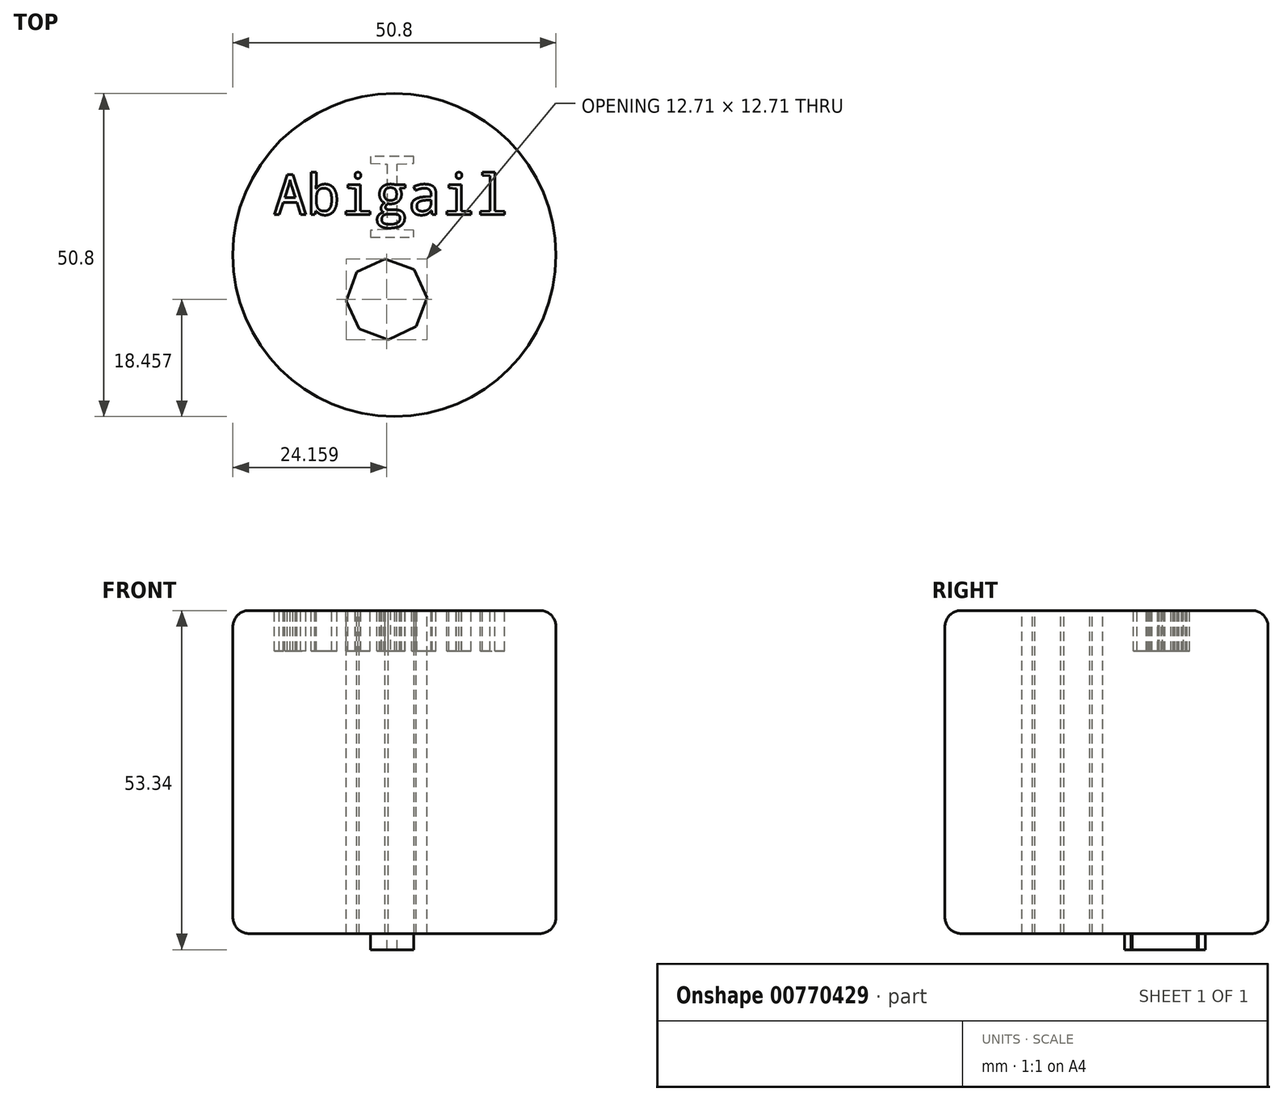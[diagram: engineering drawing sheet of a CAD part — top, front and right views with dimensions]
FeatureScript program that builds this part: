
annotation { "Feature Type Name" : "Feature", "Feature Type Description" : "" }
export const myFeature = defineFeature(function(context is Context, id is Id, definition is map)
    precondition{}
    {
        {
            var Q0;
            Q0=qCreatedBy(makeId("Top.planeOp"),FACE);
            var sketch = newSketch(context, id + "F0", { "sketchPlane" : qUnion([Q0])});
            skCircle(sketch, "E0", {"center": v(0, 0) * mm, "radius": 25.4 * mm});
            skSolve(sketch);
        }
        {
            var Q0;
            Q0 = qSketchRegion(id + "F0", true);
            extrude(context, id + "F1", {"entities" : qUnion([Q0]), "depth" : 50.8 * mm, "offsetDistance" : 25.4 * mm});
        }
        {
            var Q0;
            Q0=makeQuery(id+"F1.opExtrude","CAP_FACE",FACE,{"disambiguationData":[OSD([sQuery(id+"F0.wireOp",EDGE,"E0")])],"isStart":false});
            var sketch = newSketch(context, id + "F2", { "sketchPlane" : qUnion([Q0])});
            skText(sketch, "E1", { "text": "Abigail", "fontName": "DroidSansMono.ttf"});
            const initialGuessF2  = {"E1": [-0.01905, 0.00635, 1, 0, 0.00635]};
            skSetInitialGuess(sketch, initialGuessF2);
            skSolve(sketch);
        }
        {
            var Q0;
            Q0 = qSketchRegion(id + "F2", true);
            extrude(context, id + "F3", {"entities" : qUnion([Q0]), "operationType" : NewBodyOperationType.REMOVE, "oppositeDirection" : true, "depth" : 6.35 * mm, "offsetDistance" : 25.4 * mm});
        }
        {
            var Q0;
            {var subQ0=sQuery(id+"F0.wireOp",EDGE,"E0");Q0=makeQuery(id+"F3.boolean.opBoolean","SPLIT",FACE,{"disambiguationData":[TD([makeQuery(id+"F1.opExtrude","SWEPT_FACE",FACE,{"disambiguationData":[OSD([subQ0])]})])],"derivedFrom":makeQuery(id+"F1.opExtrude","CAP_FACE",FACE,{"disambiguationData":[OSD([subQ0])],"isStart":false})});}
            var sketch = newSketch(context, id + "F4", { "sketchPlane" : qUnion([Q0])});
            skCircle(sketch, "E2.cCircle", {"center": v(-1.24, -6.94) * mm, "radius": 5.88 * mm, "construction": true});
            skLineSegment(sketch, "E2.0", {"start": v(5.11, -6.68) * mm, "end": v(3.44, -11.25) * mm});
            skLineSegment(sketch, "E2.1", {"start": v(3.44, -11.25) * mm, "end": v(-0.98, -13.3) * mm});
            skLineSegment(sketch, "E2.2", {"start": v(-0.98, -13.3) * mm, "end": v(-5.55, -11.62) * mm});
            skLineSegment(sketch, "E2.3", {"start": v(-5.55, -11.62) * mm, "end": v(-7.6, -7.2) * mm});
            skLineSegment(sketch, "E2.4", {"start": v(-7.6, -7.2) * mm, "end": v(-5.92, -2.63) * mm});
            skLineSegment(sketch, "E2.5", {"start": v(-5.92, -2.63) * mm, "end": v(-1.5, -0.59) * mm});
            skLineSegment(sketch, "E2.6", {"start": v(-1.5, -0.59) * mm, "end": v(3.07, -2.26) * mm});
            skLineSegment(sketch, "E2.7", {"start": v(3.07, -2.26) * mm, "end": v(5.11, -6.68) * mm});
            skPoint(sketch, "E2.0.midPoint", {"position": v(4.28, -8.97) * mm});
            skSolve(sketch);
        }
        {
            var Q0;
            Q0 = qSketchRegion(id + "F4", true);
            extrude(context, id + "F5", {"entities" : qUnion([Q0]), "operationType" : NewBodyOperationType.REMOVE, "endBound" : BoundingType.THROUGH_ALL, "oppositeDirection" : true, "depth" : 25.4 * mm, "offsetDistance" : 25.4 * mm});
        }
        {
            var Q0;
            Q0=makeQuery(id+"F1.opExtrude","CAP_EDGE",EDGE,{"disambiguationData":[OSD([sQuery(id+"F0.wireOp",EDGE,"E0")])],"isStart":false});
            var Q1;
            Q1=makeQuery(id+"F1.opExtrude","CAP_EDGE",EDGE,{"disambiguationData":[OSD([sQuery(id+"F0.wireOp",EDGE,"E0")])],"isStart":true});
            fillet(context, id + "F6", {"entities" : qUnion([Q0, Q1]), "radius" : 2.54 * mm, "tangentPropagation" : true, "allowEdgeOverflow" : false});
        }
        {
            var Q0;
            Q0=makeQuery(id+"F1.opExtrude","CAP_FACE",FACE,{"disambiguationData":[OSD([sQuery(id+"F0.wireOp",EDGE,"E0")])],"isStart":true});
            var sketch = newSketch(context, id + "F7", { "sketchPlane" : qUnion([Q0])});
            skText(sketch, "E3", { "text": "I", "fontName": "DroidSansMono.ttf"});
            const initialGuessF7  = {"E3": [-0.0057, -0.01553, 1, 0, 0.01284]};
            skSetInitialGuess(sketch, initialGuessF7);
            skSolve(sketch);
        }
        {
            var Q0;
            Q0 = qSketchRegion(id + "F7", true);
            extrude(context, id + "F8", {"entities" : qUnion([Q0]), "operationType" : NewBodyOperationType.ADD, "depth" : 2.54 * mm, "offsetDistance" : 25.4 * mm});
        }
    });
